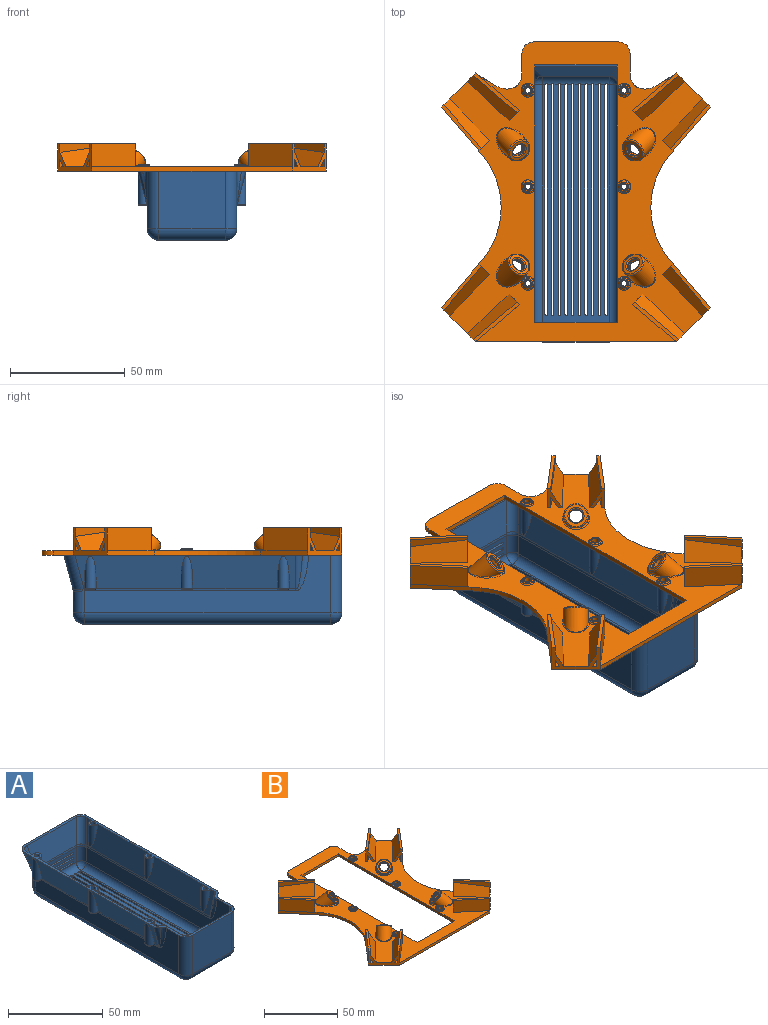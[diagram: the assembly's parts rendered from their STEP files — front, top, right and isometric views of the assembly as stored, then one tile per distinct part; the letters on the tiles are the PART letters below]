
ASSEMBLY  parts=2 mates=1
PART A: 153 faces, bbox 48.2x122x33.2 mm
  f0: plane 122.02x48.02mm, normal (0,0,1), area 491.4mm2, adj f5,f6,f7,f8,f9,f10,f11,f13
  f1: cylinder r=3mm len=92mm, axis (0,1,0), area 67.8mm2, adj f6,f7,f34,f35,f133,f136,f139,f150
  f2: cylinder r=3mm len=92mm, axis (0,1,0), area 67.8mm2, adj f5,f9,f26,f27,f124,f127,f130,f147
  f3: plane 107x29mm, normal (0,0,-1), area 2099.1mm2, adj f16,f17,f21,f22,f84,f85,f86,f88
  f4: plane 29x9.61mm, normal (0,1,0), area 188.8mm2, adj f12,f15,f16,f30,f71,f72,f73,f74
  f5: plane 107x25mm, normal (-1,0,0), area 1195.5mm2, adj f0,f2,f12,f17,f18,f26
  f6: plane 107x25mm, normal (1,0,0), area 1195.5mm2, adj f0,f1,f15,f21,f24,f35
  f7: plane 96.17x14.64mm, normal (0.97,0,-0.26), area 1239.1mm2, adj f0,f1,f13,f33,f34,f134,f137,f140
  f8: plane 37.34x14.64mm, normal (0,0.97,-0.26), area 506mm2, adj f0,f11,f13,f29,f30,f31
  f9: plane 96.17x14.64mm, normal (-0.97,0,-0.26), area 1239.1mm2, adj f0,f2,f11,f25,f27,f125,f128,f131
  f10: plane 29x25mm, normal (0,-1,0), area 725mm2, adj f0,f18,f22,f24
  f11: cylinder r=5mm len=15.11mm, axis (0.25,-0.25,-0.94), area 117.7mm2, adj f0,f8,f9,f28
  f12: cylinder r=5mm len=9.61mm, axis (0,0,1), area 73.4mm2, adj f4,f5,f14,f27,f28,f29
  f13: cylinder r=5mm len=15.11mm, axis (-0.25,-0.25,-0.94), area 117.7mm2, adj f0,f7,f8,f32
  f14: sphere r=5mm, area 53.5mm2, adj f12,f16,f17
  f15: cylinder r=5mm len=9.61mm, axis (0,0,-1), area 73.4mm2, adj f4,f6,f19,f31,f32,f34
  f16: cylinder r=5mm len=29mm, axis (-1,0,0), area 223.8mm2, adj f3,f4,f14,f19,f83,f87,f91,f95
  f17: cylinder r=5mm len=107mm, axis (0,-1,0), area 840.4mm2, adj f3,f5,f14,f20
  f18: cylinder r=5mm len=25mm, axis (0,0,-1), area 196.3mm2, adj f0,f5,f10,f20
  f19: sphere r=5mm, area 25mm2, adj f15,f16,f21
  f20: sphere r=5mm, area 27.2mm2, adj f17,f18,f22
  f21: cylinder r=5mm len=107mm, axis (0,1,0), area 840.4mm2, adj f3,f6,f19,f23
  f22: cylinder r=5mm len=29mm, axis (-1,0,0), area 227.8mm2, adj f3,f10,f20,f23
  f23: sphere r=5mm, area 39.3mm2, adj f21,f22,f24
  f24: cylinder r=5mm len=25mm, axis (0,0,-1), area 196.3mm2, adj f0,f6,f10,f23
  f25: cylinder r=3mm len=15.12mm, axis (0.26,0,-0.97), area 35.5mm2, adj f0,f9,f26
  f26: bspline ~17.47x6.37mm, area 38.7mm2, adj f0,f2,f5,f25
  f27: bspline ~0.79x0.27mm, area 0.2mm2, adj f2,f9,f12,f28
  f28: bspline ~5.26x5.26mm, area 7.4mm2, adj f11,f12,f27,f29
  f29: bspline ~0.79x0.27mm, area 0.2mm2, adj f8,f12,f28,f30
  f30: cylinder r=3mm len=29mm, axis (-1,0,0), area 22.7mm2, adj f4,f8,f29,f31
  f31: bspline ~0.79x0.27mm, area 0.2mm2, adj f8,f15,f30,f32
  f32: bspline ~5.26x5.26mm, area 7.4mm2, adj f13,f15,f31,f34
  f33: cylinder r=3mm len=15.12mm, axis (-0.26,0,-0.97), area 35.5mm2, adj f0,f7,f35
  f34: bspline ~0.79x0.27mm, area 0.2mm2, adj f1,f7,f15,f32
  f35: bspline ~17.47x6.37mm, area 38.7mm2, adj f0,f1,f6,f33
  f36: plane 29x9.61mm, normal (0,-1,0), area 188.8mm2, adj f45,f48,f49,f64,f71,f72,f73,f74
  f37: plane 107x25mm, normal (1,0,0), area 1195.5mm2, adj f0,f45,f50,f51,f59,f60
  f38: plane 107x25mm, normal (-1,0,0), area 1195.5mm2, adj f0,f48,f54,f57,f69,f70
  f39: plane 107x29mm, normal (0,0,1), area 2099.1mm2, adj f49,f50,f54,f55,f84,f85,f86,f88
  f40: plane 96.08x14.3mm, normal (-0.97,0,0.26), area 1208.4mm2, adj f0,f46,f67,f68,f70,f132,f135,f138
  f41: plane 37.16x14.3mm, normal (0,-0.97,0.26), area 493.1mm2, adj f0,f44,f46,f63,f64,f65
  f42: plane 96.08x14.3mm, normal (0.97,0,0.26), area 1208.4mm2, adj f0,f44,f58,f60,f61,f123,f126,f129
  f43: plane 29x25mm, normal (0,1,0), area 725mm2, adj f0,f51,f55,f57
  f44: cylinder r=3.7mm len=14.65mm, axis (0.25,-0.25,-0.94), area 85.1mm2, adj f0,f41,f42,f62
  f45: cylinder r=3.7mm len=9.61mm, axis (0,0,1), area 54.3mm2, adj f36,f37,f47,f61,f62,f63
  f46: cylinder r=3.7mm len=14.65mm, axis (-0.25,-0.25,-0.94), area 85.1mm2, adj f0,f40,f41,f66
  f47: sphere r=3.7mm, area 29.3mm2, adj f45,f49,f50
  f48: cylinder r=3.7mm len=9.61mm, axis (0,0,-1), area 54.3mm2, adj f36,f38,f52,f65,f66,f68
  f49: cylinder r=3.7mm len=29mm, axis (-1,0,0), area 164.6mm2, adj f36,f39,f47,f52,f83,f87,f91,f95
  f50: cylinder r=3.7mm len=107mm, axis (0,-1,0), area 621.9mm2, adj f37,f39,f47,f53
  f51: cylinder r=3.7mm len=25mm, axis (0,0,-1), area 145.3mm2, adj f0,f37,f43,f53
  f52: sphere r=3.7mm, area 13.7mm2, adj f48,f49,f54
  f53: sphere r=3.7mm, area 21.5mm2, adj f50,f51,f55
  f54: cylinder r=3.7mm len=107mm, axis (0,1,0), area 621.9mm2, adj f38,f39,f52,f56
  f55: cylinder r=3.7mm len=29mm, axis (-1,0,0), area 168.5mm2, adj f39,f43,f53,f56
  f56: sphere r=3.7mm, area 21.5mm2, adj f54,f55,f57
  f57: cylinder r=3.7mm len=25mm, axis (0,0,-1), area 145.3mm2, adj f0,f38,f43,f56
  f58: cylinder r=1.7mm len=14.57mm, axis (0.26,0,-0.97), area 19.6mm2, adj f0,f42,f59
  f59: bspline ~17.55x6.37mm, area 54.1mm2, adj f0,f37,f58,f60
  f60: cylinder r=4.3mm len=92mm, axis (0,1,0), area 103.1mm2, adj f37,f42,f59,f61
  f61: bspline ~1.12x0.27mm, area 0.2mm2, adj f42,f45,f60,f62
  f62: bspline ~3.96x3.96mm, area 7.8mm2, adj f44,f45,f61,f63
  f63: bspline ~1.12x0.27mm, area 0.2mm2, adj f41,f45,f62,f64
  f64: cylinder r=4.3mm len=29mm, axis (-1,0,0), area 32.5mm2, adj f36,f41,f63,f65
  f65: bspline ~1.12x0.27mm, area 0.2mm2, adj f41,f48,f64,f66
  f66: bspline ~3.96x3.96mm, area 7.8mm2, adj f46,f48,f65,f68
  f67: cylinder r=1.7mm len=14.57mm, axis (-0.26,0,-0.97), area 19.6mm2, adj f0,f40,f69
  f68: bspline ~1.12x0.27mm, area 0.2mm2, adj f40,f48,f66,f70
  f69: bspline ~17.55x6.37mm, area 54.1mm2, adj f0,f38,f67,f70
  f70: cylinder r=4.3mm len=92mm, axis (0,1,0), area 103.1mm2, adj f38,f40,f68,f69
  f71: cylinder r=0.6mm len=1.3mm, axis (0,1,0), area 2.5mm2, adj f4,f36,f72,f74
  f72: plane 24x1.3mm, normal (0,0,1), area 31.2mm2, adj f4,f36,f71,f73
  f73: cylinder r=0.6mm len=1.3mm, axis (0,1,0), area 2.5mm2, adj f4,f36,f72,f74
  f74: plane 24x1.3mm, normal (0,0,-1), area 31.2mm2, adj f4,f36,f71,f73
  f75: cylinder r=0.6mm len=1.3mm, axis (0,1,0), area 2.5mm2, adj f4,f36,f76,f78
  f76: plane 24x1.3mm, normal (0,0,1), area 31.2mm2, adj f4,f36,f75,f77
  f77: cylinder r=0.6mm len=1.3mm, axis (0,1,0), area 2.5mm2, adj f4,f36,f76,f78
  f78: plane 24x1.3mm, normal (0,0,-1), area 31.2mm2, adj f4,f36,f75,f77
  f79: cylinder r=0.6mm len=1.3mm, axis (0,1,0), area 2.5mm2, adj f4,f36,f80,f82
  f80: plane 24x1.3mm, normal (0,0,1), area 31.2mm2, adj f4,f36,f79,f81
  f81: cylinder r=0.6mm len=1.3mm, axis (0,1,0), area 2.5mm2, adj f4,f36,f80,f82
  f82: plane 24x1.3mm, normal (0,0,-1), area 31.2mm2, adj f4,f36,f79,f81
  f83: cylinder r=0.5mm len=1.3mm, axis (0,0,-1), area 2mm2, adj f16,f49,f84,f85
  f84: plane 100x1.3mm, normal (1,0,0), area 130mm2, adj f3,f39,f83,f86
  f85: plane 100x1.3mm, normal (-1,0,0), area 130mm2, adj f3,f39,f83,f86
  f86: cylinder r=0.5mm len=1.3mm, axis (0,0,-1), area 2mm2, adj f3,f39,f84,f85
  f87: cylinder r=0.5mm len=1.3mm, axis (0,0,-1), area 2mm2, adj f16,f49,f88,f89
  f88: plane 100x1.3mm, normal (1,0,0), area 130mm2, adj f3,f39,f87,f90
  f89: plane 100x1.3mm, normal (-1,0,0), area 130mm2, adj f3,f39,f87,f90
  f90: cylinder r=0.5mm len=1.3mm, axis (0,0,-1), area 2mm2, adj f3,f39,f88,f89
  f91: cylinder r=0.5mm len=1.3mm, axis (0,0,-1), area 2mm2, adj f16,f49,f92,f93
  f92: plane 100x1.3mm, normal (1,0,0), area 130mm2, adj f3,f39,f91,f94
  f93: plane 100x1.3mm, normal (-1,0,0), area 130mm2, adj f3,f39,f91,f94
  f94: cylinder r=0.5mm len=1.3mm, axis (0,0,-1), area 2mm2, adj f3,f39,f92,f93
  f95: cylinder r=0.5mm len=1.3mm, axis (0,0,-1), area 2mm2, adj f16,f49,f96,f97
  f96: plane 100x1.3mm, normal (1,0,0), area 130mm2, adj f3,f39,f95,f98
  f97: plane 100x1.3mm, normal (-1,0,0), area 130mm2, adj f3,f39,f95,f98
  f98: cylinder r=0.5mm len=1.3mm, axis (0,0,-1), area 2mm2, adj f3,f39,f96,f97
  f99: cylinder r=0.5mm len=1.3mm, axis (0,0,-1), area 2mm2, adj f16,f49,f100,f101
  f100: plane 100x1.3mm, normal (1,0,0), area 130mm2, adj f3,f39,f99,f102
  f101: plane 100x1.3mm, normal (-1,0,0), area 130mm2, adj f3,f39,f99,f102
  f102: cylinder r=0.5mm len=1.3mm, axis (0,0,-1), area 2mm2, adj f3,f39,f100,f101
  f103: cylinder r=0.5mm len=1.3mm, axis (0,0,-1), area 2mm2, adj f16,f49,f104,f105
  f104: plane 100x1.3mm, normal (1,0,0), area 130mm2, adj f3,f39,f103,f106
  f105: plane 100x1.3mm, normal (-1,0,0), area 130mm2, adj f3,f39,f103,f106
  f106: cylinder r=0.5mm len=1.3mm, axis (0,0,-1), area 2mm2, adj f3,f39,f104,f105
  f107: cylinder r=0.5mm len=1.3mm, axis (0,0,-1), area 2mm2, adj f16,f49,f108,f109
  f108: plane 100x1.3mm, normal (1,0,0), area 130mm2, adj f3,f39,f107,f110
  f109: plane 100x1.3mm, normal (-1,0,0), area 130mm2, adj f3,f39,f107,f110
  f110: cylinder r=0.5mm len=1.3mm, axis (0,0,-1), area 2mm2, adj f3,f39,f108,f109
  f111: cylinder r=0.5mm len=1.3mm, axis (0,0,-1), area 2mm2, adj f16,f49,f112,f113
  f112: plane 100x1.3mm, normal (1,0,0), area 130mm2, adj f3,f39,f111,f114
  f113: plane 100x1.3mm, normal (-1,0,0), area 130mm2, adj f3,f39,f111,f114
  f114: cylinder r=0.5mm len=1.3mm, axis (0,0,-1), area 2mm2, adj f3,f39,f112,f113
  f115: cylinder r=0.5mm len=1.3mm, axis (0,0,-1), area 2mm2, adj f16,f49,f116,f117
  f116: plane 100x1.3mm, normal (1,0,0), area 130mm2, adj f3,f39,f115,f118
  f117: plane 100x1.3mm, normal (-1,0,0), area 130mm2, adj f3,f39,f115,f118
  f118: cylinder r=0.5mm len=1.3mm, axis (0,0,-1), area 2mm2, adj f3,f39,f116,f117
  f119: cylinder r=0.5mm len=1.3mm, axis (0,0,-1), area 2mm2, adj f16,f49,f120,f121
  f120: plane 100x1.3mm, normal (1,0,0), area 130mm2, adj f3,f39,f119,f122
  f121: plane 100x1.3mm, normal (-1,0,0), area 130mm2, adj f3,f39,f119,f122
  f122: cylinder r=0.5mm len=1.3mm, axis (0,0,-1), area 2mm2, adj f3,f39,f120,f121
  f123: cylinder r=2.5mm len=14.12mm, axis (0,0,-1), area 89.7mm2, adj f0,f42
  f124: plane 4x3.38mm, normal (0,0,-1), area 6.4mm2, adj f2,f146,f148
  f125: cylinder r=2.5mm len=14.2mm, axis (0,0,-1), area 90.5mm2, adj f9,f148
  f126: cylinder r=2.5mm len=14.12mm, axis (0,0,-1), area 89.7mm2, adj f0,f42
  f127: plane 4x3.38mm, normal (0,0,-1), area 6.4mm2, adj f2,f145,f149
  f128: cylinder r=2.5mm len=14.2mm, axis (0,0,-1), area 90.5mm2, adj f9,f149
  f129: cylinder r=2.5mm len=14.12mm, axis (0,0,-1), area 89.7mm2, adj f0,f42
  f130: plane 4x3.38mm, normal (0,0,-1), area 6.4mm2, adj f2,f144,f147
  f131: cylinder r=2.5mm len=14.2mm, axis (0,0,-1), area 90.5mm2, adj f9,f147
  f132: cylinder r=2.5mm len=14.12mm, axis (0,0,-1), area 89.7mm2, adj f0,f40
  f133: plane 4x3.38mm, normal (0,0,-1), area 6.4mm2, adj f1,f143,f150
  f134: cylinder r=2.5mm len=14.2mm, axis (0,0,-1), area 90.5mm2, adj f7,f150
  f135: cylinder r=2.5mm len=14.12mm, axis (0,0,-1), area 89.7mm2, adj f0,f40
  f136: plane 4x3.38mm, normal (0,0,-1), area 6.4mm2, adj f1,f142,f151
  f137: cylinder r=2.5mm len=14.2mm, axis (0,0,-1), area 90.5mm2, adj f7,f151
  f138: cylinder r=2.5mm len=14.12mm, axis (0,0,-1), area 89.7mm2, adj f0,f40
  f139: plane 4x3.38mm, normal (0,0,-1), area 6.4mm2, adj f1,f141,f152
  f140: cylinder r=2.5mm len=14.2mm, axis (0,0,-1), area 90.5mm2, adj f7,f152
  f141: cylinder r=1.25mm len=15mm, axis (0,0,-1), area 117.8mm2, adj f0,f139
  f142: cylinder r=1.25mm len=15mm, axis (0,0,-1), area 117.8mm2, adj f0,f136
  f143: cylinder r=1.25mm len=15mm, axis (0,0,-1), area 117.8mm2, adj f0,f133
  f144: cylinder r=1.25mm len=15mm, axis (0,0,-1), area 117.8mm2, adj f0,f130
  f145: cylinder r=1.25mm len=15mm, axis (0,0,-1), area 117.8mm2, adj f0,f127
  f146: cylinder r=1.25mm len=15mm, axis (0,0,-1), area 117.8mm2, adj f0,f124
  f147: torus R=2mm, axis (0,0,-1), area 8mm2, adj f2,f9,f130,f131
  f148: torus R=2mm, axis (0,0,-1), area 8mm2, adj f2,f9,f124,f125
  f149: torus R=2mm, axis (0,0,-1), area 8mm2, adj f2,f9,f127,f128
  f150: torus R=2mm, axis (0,0,-1), area 8mm2, adj f1,f7,f133,f134
  f151: torus R=2mm, axis (0,0,-1), area 8mm2, adj f1,f7,f136,f137
  f152: torus R=2mm, axis (0,0,-1), area 8mm2, adj f1,f7,f139,f140
PART B: 164 faces, bbox 117x130.5x18.3 mm
  f0: plane 130.5x114.87mm, normal (0,0,1), area 5361.3mm2, adj f1,f2,f6,f9,f10,f11,f12,f13
  f1: plane 20.42x18.52mm, normal (0.63,0.6,-0.5), area 126.8mm2, adj f0,f141,f142,f143
  f2: plane 21.65x19.74mm, normal (-0.63,-0.6,0.5), area 213.4mm2, adj f0,f3,f141,f143
  f3: plane 19.09x16.26mm, normal (-0.76,-0.65,0), area 64.7mm2, adj f2,f4,f141,f143
  f4: plane 20.15x17.32mm, normal (0,0,1), area 37.5mm2, adj f3,f5,f141,f143
  f5: plane 19.09x16.27mm, normal (0.76,0.65,0), area 250.1mm2, adj f4,f140,f141,f143
  f6: plane 21.65x19.74mm, normal (0.6,0.63,0.5), area 213.4mm2, adj f0,f7,f11,f143
  f7: plane 19.09x16.26mm, normal (0.65,0.76,0), area 64.7mm2, adj f6,f8,f11,f143
  f8: plane 20.15x17.32mm, normal (0,0,1), area 37.5mm2, adj f7,f11,f12,f143
  f9: plane 20.42x18.52mm, normal (-0.6,-0.63,-0.5), area 126.8mm2, adj f0,f10,f11,f143
  f10: plane 19.09x16.26mm, normal (0.65,0.76,0), area 110.1mm2, adj f0,f9,f11,f143
  f11: plane 9.97x4.54mm, normal (-0.71,0.71,0), area 27.1mm2, adj f0,f6,f7,f8,f9,f10,f12
  f12: plane 19.09x16.26mm, normal (-0.65,-0.76,0), area 250.1mm2, adj f0,f8,f11,f143
  f13: plane 87.3x2mm, normal (0,-1,0), area 174.6mm2, adj f0,f14,f95,f143
  f14: plane 130.5x117mm, normal (0,0,-1), area 6276.8mm2, adj f13,f15,f20,f25,f30,f35,f40,f45
  f15: cylinder r=1.5mm len=3mm, axis (0,0,-1), area 28.3mm2, adj f14,f16
  f16: plane 4x4mm, normal (0,0,1), area 5.5mm2, adj f15,f17
  f17: torus R=2mm, axis (0,0,1), area 11.4mm2, adj f16,f18,f157
  f18: cylinder r=2.5mm len=1.25mm, axis (0,0,-1), area 0mm2, adj f17,f19
  f19: bspline ~1.78x0.55mm, area 1mm2, adj f18,f156,f157
  f20: cylinder r=1.5mm len=3mm, axis (0,0,-1), area 28.3mm2, adj f14,f21
  f21: plane 4x4mm, normal (0,0,1), area 5.5mm2, adj f20,f22
  f22: torus R=2mm, axis (0,0,1), area 11.4mm2, adj f21,f23,f145
  f23: cylinder r=2.5mm len=1.25mm, axis (0,0,-1), area 0mm2, adj f22,f24
  f24: bspline ~1.78x0.55mm, area 1mm2, adj f23,f145,f156
  f25: cylinder r=1.5mm len=3mm, axis (0,0,-1), area 28.3mm2, adj f14,f26
  f26: plane 4x4mm, normal (0,0,1), area 5.5mm2, adj f25,f27
  f27: torus R=2mm, axis (0,0,1), area 11.4mm2, adj f26,f28,f146
  f28: cylinder r=2.5mm len=1.25mm, axis (0,0,-1), area 0mm2, adj f27,f29
  f29: bspline ~1.78x0.55mm, area 1mm2, adj f28,f146,f156
  f30: cylinder r=1.5mm len=3mm, axis (0,0,-1), area 28.3mm2, adj f14,f31
  f31: plane 4x4mm, normal (0,0,1), area 5.5mm2, adj f30,f32
  f32: torus R=2mm, axis (0,0,1), area 11.4mm2, adj f31,f33,f34,f153
  f33: cylinder r=2.5mm len=0.63mm, axis (0,0,-1), area 0mm2, adj f32,f34
  f34: bspline ~1.78x0.55mm, area 1mm2, adj f32,f33,f153,f154
  f35: cylinder r=1.5mm len=3mm, axis (0,0,-1), area 28.3mm2, adj f14,f36
  f36: plane 4x4mm, normal (0,0,1), area 5.5mm2, adj f35,f37
  f37: torus R=2mm, axis (0,0,1), area 11.4mm2, adj f36,f38,f39,f149
  f38: cylinder r=2.5mm len=0.63mm, axis (0,0,-1), area 0mm2, adj f37,f39
  f39: bspline ~1.78x0.55mm, area 1mm2, adj f37,f38,f149,f154
  f40: cylinder r=1.5mm len=3mm, axis (0,0,-1), area 28.3mm2, adj f14,f41
  f41: plane 4x4mm, normal (0,0,1), area 5.5mm2, adj f40,f42
  f42: torus R=2mm, axis (0,0,1), area 11.4mm2, adj f41,f43,f44,f148
  f43: cylinder r=2.5mm len=0.63mm, axis (0,0,-1), area 0mm2, adj f42,f44
  f44: bspline ~1.78x0.55mm, area 1mm2, adj f42,f43,f148,f154
  f45: bspline ~12.5x12.5mm, area 29mm2, adj f14,f46
  f46: cylinder r=4.6mm len=15.05mm, axis (-0.5,0.5,-0.71), area 201.5mm2, adj f45,f47
  f47: plane 7.97x7.97mm, normal (-0.5,0.5,-0.71), area 28mm2, adj f46,f48
  f48: torus R=3.5mm, axis (-0.5,0.5,-0.71), area 15.7mm2, adj f47,f49
  f49: cylinder r=3mm len=5.45mm, axis (-0.5,0.5,-0.71), area 9.4mm2, adj f48,f50
  f50: torus R=3.5mm, axis (0.5,-0.5,0.71), area 15.7mm2, adj f49,f51
  f51: plane 8.4x8.4mm, normal (0.5,-0.5,0.71), area 35.4mm2, adj f50,f52
  f52: torus R=4.85mm, axis (0.5,-0.5,0.71), area 24.5mm2, adj f51,f53,f160
  f53: cylinder r=5.35mm len=14.94mm, axis (-0.5,0.5,-0.71), area 175.8mm2, adj f52,f161
  f54: bspline ~12.5x12.5mm, area 29mm2, adj f14,f55
  f55: cylinder r=4.6mm len=15.05mm, axis (0.5,0.5,-0.71), area 201.5mm2, adj f54,f56
  f56: plane 7.97x7.97mm, normal (0.5,0.5,-0.71), area 28mm2, adj f55,f57
  f57: torus R=3.5mm, axis (0.5,0.5,-0.71), area 15.7mm2, adj f56,f58
  f58: cylinder r=3mm len=5.45mm, axis (0.5,0.5,-0.71), area 9.4mm2, adj f57,f59
  f59: torus R=3.5mm, axis (-0.5,-0.5,0.71), area 15.7mm2, adj f58,f60
  f60: plane 8.4x8.4mm, normal (-0.5,-0.5,0.71), area 35.4mm2, adj f59,f61
  f61: torus R=4.85mm, axis (-0.5,-0.5,0.71), area 24.5mm2, adj f60,f62,f162
  f62: cylinder r=5.35mm len=14.94mm, axis (0.5,0.5,-0.71), area 175.8mm2, adj f61,f163
  f63: bspline ~12.5x12.5mm, area 29mm2, adj f14,f64
  f64: cylinder r=4.6mm len=15.05mm, axis (0.5,-0.5,-0.71), area 201.5mm2, adj f63,f65
  f65: plane 7.97x7.97mm, normal (0.5,-0.5,-0.71), area 28mm2, adj f64,f66
  f66: torus R=3.5mm, axis (0.5,-0.5,-0.71), area 15.7mm2, adj f65,f67
  f67: cylinder r=3mm len=5.45mm, axis (0.5,-0.5,-0.71), area 9.4mm2, adj f66,f68
  f68: torus R=3.5mm, axis (-0.5,0.5,0.71), area 15.7mm2, adj f67,f69
  f69: plane 8.4x8.4mm, normal (-0.5,0.5,0.71), area 35.4mm2, adj f68,f70
  f70: torus R=4.85mm, axis (-0.5,0.5,0.71), area 24.5mm2, adj f69,f71,f159
  f71: cylinder r=5.35mm len=14.93mm, axis (0.5,-0.5,-0.71), area 176.8mm2, adj f70,f72,f144,f158
  f72: bspline ~2.26x2.1mm, area 1.4mm2, adj f71,f144,f157,f158
  f73: bspline ~12.5x12.5mm, area 29mm2, adj f14,f74
  f74: cylinder r=4.6mm len=15.05mm, axis (-0.5,-0.5,-0.71), area 201.5mm2, adj f73,f75
  f75: plane 7.97x7.97mm, normal (-0.5,-0.5,-0.71), area 28mm2, adj f74,f76
  f76: torus R=3.5mm, axis (-0.5,-0.5,-0.71), area 15.7mm2, adj f75,f77
  f77: cylinder r=3mm len=5.45mm, axis (-0.5,-0.5,-0.71), area 9.4mm2, adj f76,f78
  f78: torus R=3.5mm, axis (0.5,0.5,0.71), area 15.7mm2, adj f77,f79
  f79: plane 8.4x8.4mm, normal (0.5,0.5,0.71), area 35.4mm2, adj f78,f80
  f80: torus R=4.85mm, axis (0.5,0.5,0.71), area 24.5mm2, adj f79,f81,f151
  f81: cylinder r=5.35mm len=14.93mm, axis (-0.5,-0.5,-0.71), area 176.8mm2, adj f80,f82,f150,f152
  f82: bspline ~2.31x2.15mm, area 1.4mm2, adj f81,f150,f152,f153
  f83: plane 19.09x16.26mm, normal (0.65,-0.76,0), area 250.1mm2, adj f0,f84,f88,f95
  f84: plane 20.15x17.32mm, normal (0,0,1), area 37.5mm2, adj f83,f85,f88,f95
  f85: plane 19.09x16.26mm, normal (-0.65,0.76,0), area 64.7mm2, adj f84,f88,f89,f95
  f86: plane 19.09x16.26mm, normal (-0.65,0.76,0), area 110.1mm2, adj f0,f87,f88,f95
  f87: plane 20.42x18.52mm, normal (0.6,-0.63,-0.5), area 126.8mm2, adj f0,f86,f88,f95
  f88: plane 9.97x4.54mm, normal (0.71,0.71,0), area 27.1mm2, adj f0,f83,f84,f85,f86,f87,f89
  f89: plane 21.65x19.74mm, normal (-0.6,0.63,0.5), area 213.4mm2, adj f0,f85,f88,f95
  f90: plane 21.65x19.74mm, normal (0.63,-0.6,0.5), area 213.4mm2, adj f0,f91,f95,f97
  f91: plane 19.09x16.26mm, normal (0.76,-0.65,0), area 64.7mm2, adj f90,f92,f95,f97
  f92: plane 20.15x17.32mm, normal (0,0,1), area 37.5mm2, adj f91,f93,f95,f97
  f93: plane 19.1x16.27mm, normal (-0.76,0.65,0), area 250.1mm2, adj f92,f95,f97,f98
  f94: plane 20.42x18.52mm, normal (-0.63,0.6,-0.5), area 126.8mm2, adj f0,f95,f96,f97
  f95: plane 14.85x14.85mm, normal (-0.71,-0.71,0), area 88.4mm2, adj f0,f13,f14,f83,f84,f85,f86,f87
  f96: plane 19.09x16.26mm, normal (0.76,-0.65,0), area 110.1mm2, adj f0,f94,f95,f97
  f97: plane 9.97x4.54mm, normal (0.71,0.71,0), area 27.1mm2, adj f0,f90,f91,f92,f93,f94,f96
  f98: plane 20.41x17.39mm, normal (-0.76,0.65,0), area 53.6mm2, adj f0,f14,f93,f95,f99
  f99: cylinder r=35.84mm len=46.48mm, axis (0,0,-1), area 101.1mm2, adj f0,f14,f98,f100
  f100: plane 20.41x17.39mm, normal (-0.76,-0.65,0), area 53.6mm2, adj f0,f14,f99,f101,f112
  f101: plane 19.09x16.27mm, normal (-0.76,-0.65,0), area 250.1mm2, adj f100,f102,f106,f112
  f102: plane 20.15x17.32mm, normal (0,0,1), area 37.5mm2, adj f101,f103,f106,f112
  f103: plane 19.09x16.26mm, normal (0.76,0.65,0), area 64.7mm2, adj f102,f106,f107,f112
  f104: plane 19.09x16.26mm, normal (0.76,0.65,0), area 110.1mm2, adj f0,f105,f106,f112
  f105: plane 20.42x18.52mm, normal (-0.63,-0.6,-0.5), area 126.8mm2, adj f0,f104,f106,f112
  f106: plane 9.97x4.54mm, normal (0.71,-0.71,0), area 27.1mm2, adj f0,f101,f102,f103,f104,f105,f107
  f107: plane 21.65x19.74mm, normal (0.63,0.6,0.5), area 213.4mm2, adj f0,f103,f106,f112
  f108: plane 21.65x19.74mm, normal (-0.6,-0.63,0.5), area 213.4mm2, adj f0,f109,f112,f114
  f109: plane 19.09x16.26mm, normal (-0.65,-0.76,0), area 64.7mm2, adj f108,f110,f112,f114
  f110: plane 20.15x17.32mm, normal (0,0,1), area 37.5mm2, adj f109,f112,f114,f115
  f111: plane 20.42x18.52mm, normal (0.6,0.63,-0.5), area 126.8mm2, adj f0,f112,f113,f114
  f112: plane 14.85x14.85mm, normal (-0.71,0.71,0), area 88.4mm2, adj f0,f14,f100,f101,f102,f103,f104,f105
  f113: plane 19.09x16.26mm, normal (-0.65,-0.76,0), area 110.1mm2, adj f0,f111,f112,f114
  f114: plane 9.97x4.54mm, normal (0.71,-0.71,0), area 27.1mm2, adj f0,f108,f109,f110,f111,f113,f115
  f115: plane 19.09x16.26mm, normal (0.65,0.76,0), area 250.1mm2, adj f0,f110,f112,f114
  f116: extruded ~20.17x6.96mm, area 52.7mm2, adj f0,f14,f112,f117
  f117: plane 8.5x2mm, normal (-1,0,0), area 17mm2, adj f0,f14,f116,f118
  f118: cylinder r=5mm len=5mm, axis (0,0,-1), area 15.7mm2, adj f0,f14,f117,f119
  f119: plane 37x2mm, normal (0,1,0), area 74mm2, adj f0,f14,f118,f120
  f120: cylinder r=5mm len=5mm, axis (0,0,-1), area 15.7mm2, adj f0,f14,f119,f121
  f121: plane 8.5x2mm, normal (1,0,0), area 17mm2, adj f0,f14,f120,f122
  f122: extruded ~20.17x6.96mm, area 52.7mm2, adj f0,f14,f121,f135
  f123: plane 19.09x16.26mm, normal (-0.65,0.76,0), area 250.1mm2, adj f0,f124,f128,f135
  f124: plane 20.15x17.32mm, normal (0,0,1), area 37.5mm2, adj f123,f125,f128,f135
  f125: plane 19.09x16.26mm, normal (0.65,-0.76,0), area 64.7mm2, adj f124,f128,f129,f135
  f126: plane 19.09x16.26mm, normal (0.65,-0.76,0), area 110.1mm2, adj f0,f127,f128,f135
  f127: plane 20.42x18.52mm, normal (-0.6,0.63,-0.5), area 126.8mm2, adj f0,f126,f128,f135
  f128: plane 9.97x4.54mm, normal (-0.71,-0.71,0), area 27.1mm2, adj f0,f123,f124,f125,f126,f127,f129
  f129: plane 21.65x19.74mm, normal (0.6,-0.63,0.5), area 213.4mm2, adj f0,f125,f128,f135
  f130: plane 21.65x19.74mm, normal (-0.63,0.6,0.5), area 213.4mm2, adj f0,f131,f135,f137
  f131: plane 19.09x16.26mm, normal (-0.76,0.65,0), area 64.7mm2, adj f130,f132,f135,f137
  f132: plane 20.15x17.32mm, normal (0,0,1), area 37.5mm2, adj f131,f133,f135,f137
  f133: plane 19.09x16.27mm, normal (0.76,-0.65,0), area 250.1mm2, adj f132,f135,f137,f138
  f134: plane 20.42x18.52mm, normal (0.63,-0.6,-0.5), area 126.8mm2, adj f0,f135,f136,f137
  f135: plane 14.85x14.85mm, normal (0.71,0.71,0), area 88.4mm2, adj f0,f14,f122,f123,f124,f125,f126,f127
  f136: plane 19.09x16.26mm, normal (-0.76,0.65,0), area 110.1mm2, adj f0,f134,f135,f137
  f137: plane 9.97x4.54mm, normal (-0.71,-0.71,0), area 27.1mm2, adj f0,f130,f131,f132,f133,f134,f136
  f138: plane 20.41x17.39mm, normal (0.76,-0.65,0), area 53.6mm2, adj f0,f14,f133,f135,f139
  f139: cylinder r=35.84mm len=46.48mm, axis (0,0,-1), area 101.1mm2, adj f0,f14,f138,f140
  f140: plane 20.41x17.39mm, normal (0.76,0.65,0), area 53.6mm2, adj f0,f5,f14,f139,f143
  f141: plane 9.97x4.54mm, normal (-0.71,0.71,0), area 27.1mm2, adj f0,f1,f2,f3,f4,f5,f142
  f142: plane 19.09x16.26mm, normal (-0.76,-0.65,0), area 110.1mm2, adj f0,f1,f141,f143
  f143: plane 14.85x14.85mm, normal (0.71,-0.71,0), area 88.4mm2, adj f0,f1,f2,f3,f4,f5,f6,f7
  f144: bspline ~5.97x2.26mm, area 6.1mm2, adj f0,f71,f72,f159
  f145: torus R=3mm, axis (0,0,1), area 12.2mm2, adj f0,f22,f24
  f146: torus R=3mm, axis (0,0,1), area 12.2mm2, adj f0,f27,f29
  f147: plane 36x2mm, normal (0,-1,0), area 72mm2, adj f0,f14,f154,f156
  f148: torus R=3mm, axis (0,0,1), area 12.2mm2, adj f0,f42,f44
  f149: torus R=3mm, axis (0,0,1), area 12.2mm2, adj f0,f37,f39
  f150: bspline ~5.97x2.26mm, area 6.1mm2, adj f0,f81,f82,f151
  f151: bspline ~4.35x4.13mm, area 5.2mm2, adj f0,f80,f150,f152
  f152: bspline ~14.32x10.98mm, area 19.3mm2, adj f0,f81,f82,f151
  f153: torus R=3mm, axis (0,0,1), area 12.2mm2, adj f0,f32,f34,f82
  f154: plane 112.01x2.01mm, normal (1,0,0), area 224mm2, adj f0,f14,f34,f39,f44,f147,f155
  f155: plane 36x2mm, normal (0,1,0), area 72mm2, adj f0,f14,f154,f156
  f156: plane 112.01x2.01mm, normal (-1,0,0), area 224mm2, adj f0,f14,f19,f24,f29,f147,f155
  f157: torus R=3mm, axis (0,0,1), area 12.2mm2, adj f0,f17,f19,f72
  f158: bspline ~14.32x10.98mm, area 19.3mm2, adj f0,f71,f72,f159
  f159: bspline ~4.35x4.13mm, area 5.2mm2, adj f0,f70,f144,f158
  f160: bspline ~4.35x4.13mm, area 5.2mm2, adj f0,f52,f161
  f161: bspline ~14.33x14.33mm, area 27.2mm2, adj f0,f53,f160
  f162: bspline ~4.35x4.13mm, area 5.2mm2, adj f0,f61,f163
  f163: bspline ~14.33x14.33mm, area 27.2mm2, adj f0,f62,f162
PLACE A t=(0.51,-8.23,-35.64)mm
PLACE B t=(0.51,-8.23,-5.64)mm
MATE fastened A.f132 <-> B.f25  axis (0,0,1) through (21.41,42.77,-5.64)mm
